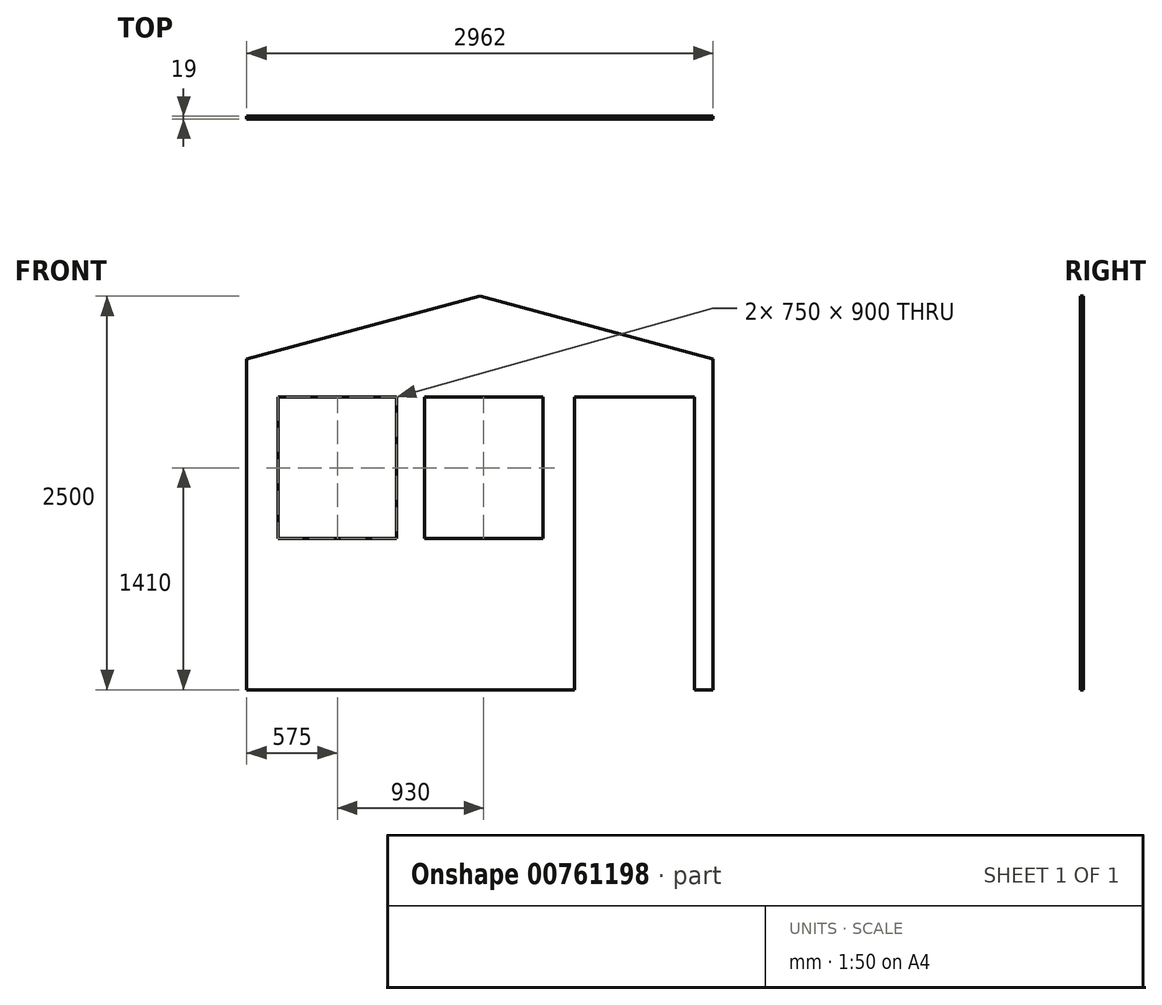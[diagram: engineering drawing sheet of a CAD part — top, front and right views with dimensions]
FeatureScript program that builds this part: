
annotation { "Feature Type Name" : "Feature", "Feature Type Description" : "" }
export const myFeature = defineFeature(function(context is Context, id is Id, definition is map)
    precondition{}
    {
        {
            var Q0;
            Q0=qCreatedBy(makeId("Front.planeOp"),FACE);
            var sketch = newSketch(context, id + "F0", { "sketchPlane" : qUnion([Q0])});
            skLineSegment(sketch, "E0.bottom", {"start": v(0, 0) * mm, "end": v(-120, 0) * mm});
            skLineSegment(sketch, "E0.left", {"start": v(0, 0) * mm, "end": v(0, 2100) * mm});
            skLineSegment(sketch, "E0.right", {"start": v(-2962, 0) * mm, "end": v(-2962, 2100) * mm});
            skLineSegment(sketch, "E1", {"start": v(0, 2100) * mm, "end": v(-1481, 2500) * mm});
            skLineSegment(sketch, "E2", {"start": v(-1481, 2500) * mm, "end": v(-2962, 2100) * mm});
            skLineSegment(sketch, "E3.top", {"start": v(-120, 1860) * mm, "end": v(-882, 1860) * mm});
            skLineSegment(sketch, "E3.left", {"start": v(-120, 0) * mm, "end": v(-120, 1860) * mm});
            skLineSegment(sketch, "E3.right", {"start": v(-882, 0) * mm, "end": v(-882, 1860) * mm});
            skLineSegment(sketch, "E4.trimOffspring", {"start": v(-882, 0) * mm, "end": v(-2962, 0) * mm});
            skLineSegment(sketch, "E5.bottom", {"start": v(-1082, 1860) * mm, "end": v(-1832, 1860) * mm});
            skLineSegment(sketch, "E5.top", {"start": v(-1082, 960) * mm, "end": v(-1832, 960) * mm});
            skLineSegment(sketch, "E5.left", {"start": v(-1082, 1860) * mm, "end": v(-1082, 960) * mm});
            skLineSegment(sketch, "E5.right", {"start": v(-1832, 1860) * mm, "end": v(-1832, 960) * mm});
            skLineSegment(sketch, "E6.bottom", {"start": v(-2012, 1860) * mm, "end": v(-2762, 1860) * mm});
            skLineSegment(sketch, "E6.top", {"start": v(-2012, 960) * mm, "end": v(-2762, 960) * mm});
            skLineSegment(sketch, "E6.left", {"start": v(-2012, 1860) * mm, "end": v(-2012, 960) * mm});
            skLineSegment(sketch, "E6.right", {"start": v(-2762, 1860) * mm, "end": v(-2762, 960) * mm});
            skSolve(sketch);
        }
        {
            var Q0;
            Q0=qSketchRegion(id+"F0",true);
            extrude(context, id + "F1", {"entities" : qUnion([Q0]), "depth" : 19 * mm, "offsetDistance" : 25 * mm});
        }
    });
